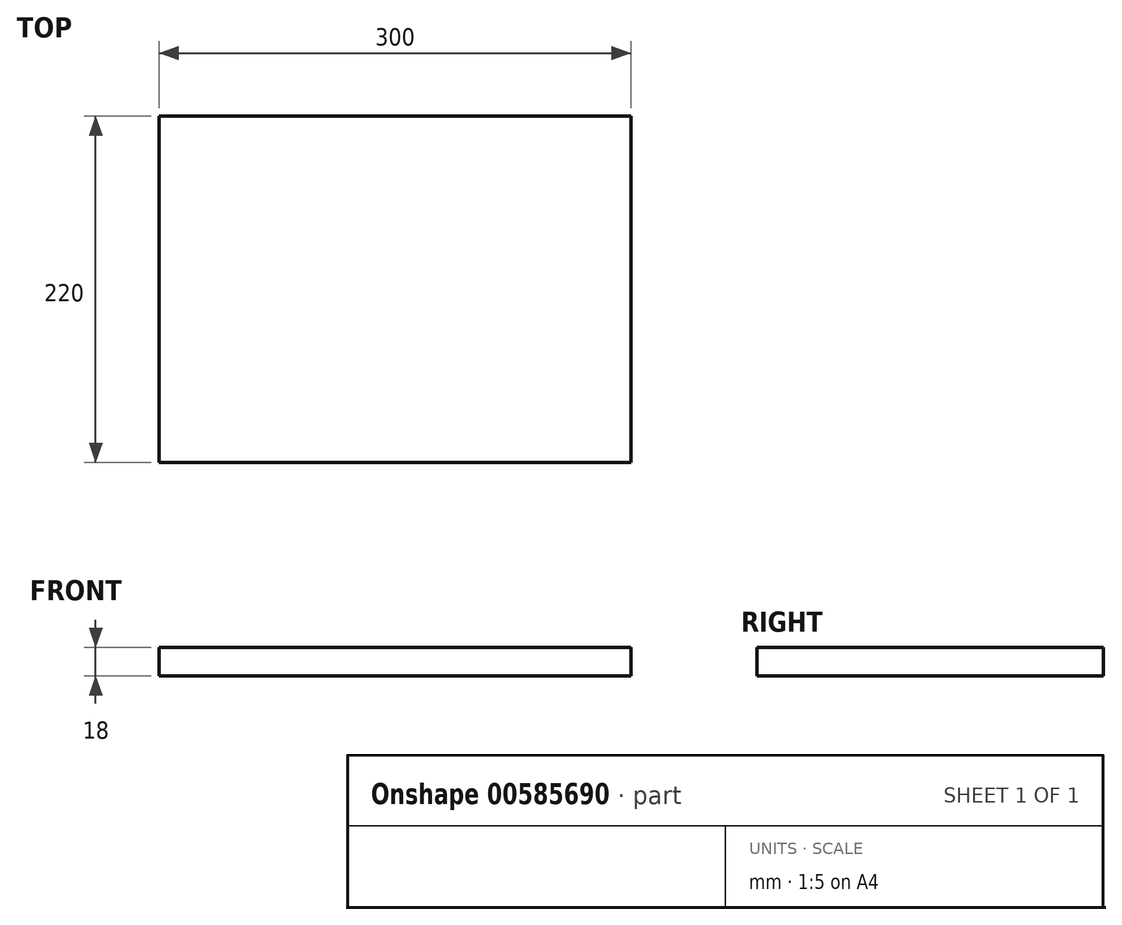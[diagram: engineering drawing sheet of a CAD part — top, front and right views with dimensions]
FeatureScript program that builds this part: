
annotation { "Feature Type Name" : "Feature", "Feature Type Description" : "" }
export const myFeature = defineFeature(function(context is Context, id is Id, definition is map)
    precondition{}
    {
        {
            var Q0;
            Q0=qCreatedBy(makeId("Top.planeOp"),FACE);
            var sketch = newSketch(context, id + "F0", { "sketchPlane" : qUnion([Q0])});
            skLineSegment(sketch, "E0.bottom", {"start": v(0, 0) * mm, "end": v(-300, 0) * mm});
            skLineSegment(sketch, "E0.top", {"start": v(0, -220) * mm, "end": v(-300, -220) * mm});
            skLineSegment(sketch, "E0.left", {"start": v(0, 0) * mm, "end": v(0, -220) * mm});
            skLineSegment(sketch, "E0.right", {"start": v(-300, 0) * mm, "end": v(-300, -220) * mm});
            skSolve(sketch);
        }
        {
            var Q0;
            Q0=makeQuery(id+"F0.imprint","IMPRINT",FACE,{"disambiguationData":[TD([[makeQuery(id+"F0.imprint","IMPRINT",EDGE,{"derivedFrom":sQuery(id+"F0.wireOp",EDGE,"E0.bottom")}),1.0]])]});
            extrude(context, id + "F1", {"entities" : qUnion([Q0]), "depth" : 18 * mm, "offsetDistance" : 25 * mm});
        }
    });
